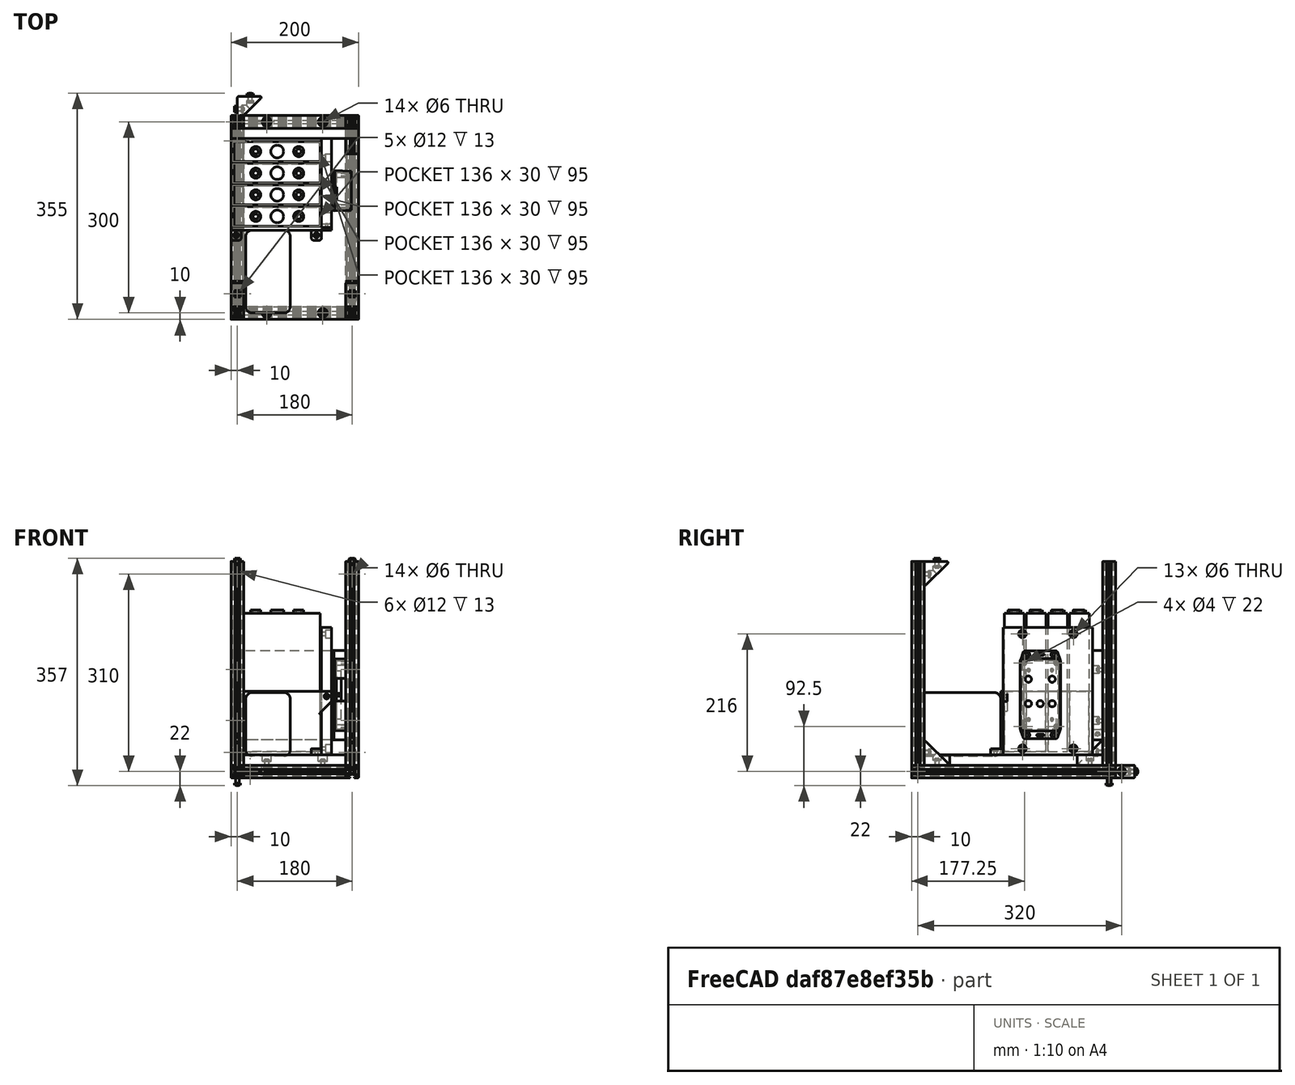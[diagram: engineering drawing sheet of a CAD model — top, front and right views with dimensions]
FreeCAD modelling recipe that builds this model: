
FCSTD DOCUMENT  (FreeCAD 0.17R9796 (Git))
Label: UPKframeNG2e
License: All rights reserved
LicenseURL: http://en.wikipedia.org/wiki/All_rights_reserved
objects: Part::Feature×64, Part::FeaturePython×24, Part::Compound×12, App::FeaturePython×8, App::Part×6, Part::Cylinder×5, Part::Box×4, Part::Cut×4, PartDesign::Body×2, PartDesign::Pocket×1, Part::Fillet×1, Part::MultiFuse×1
note: 119 computed .brp shape members not serialized (recipe doc carries the construction recipe); baked Part::Feature solids carry a one-line shape summary decoded from their .brp

FEATURE [Part::Feature] Pocket003001  label="tslot32con"
  Placement = pos=(0,10,10) rot=(1,0,0;1.5708rad)
  shape: bbox 20 x 320 x 20 mm, 150 faces (baked)
FEATURE [Part::Feature] Pocket003002  label="tslot16"
  Placement = pos=(10,0,10) rot=(0,1,0;1.5708rad)
  shape: bbox 160 x 20 x 20 mm, 94 faces (baked)
FEATURE [Part::Feature] Pocket003006  label="tslot16_001"
  Placement = pos=(10,-300,10) rot=(0,1,0;1.5708rad)
  shape: bbox 160 x 20 x 20 mm, 94 faces (baked)
FEATURE [Part::Feature] Pocket003007  label="tslot32con_001"
  Placement = pos=(180,-310,10) rot=(0,0.707107,0.707107;3.14159rad)
  shape: bbox 20 x 320 x 20 mm, 150 faces (baked)
FEATURE [Part::FeaturePython] Screw  label="M6x25-Screw"  # Fasteners workbench fastener (typed FeaturePython)
  Placement = pos=(-4,0,10) rot=(0,-1,0;1.5708rad)
  diameter = 7
  invert = false
  length = 6
  matchOuter = false
  offset = 0
  thread = false
  type = 15
FEATURE [Part::FeaturePython] Screw001  label="M6x25-Screw004"  # Fasteners workbench fastener (typed FeaturePython)
  Placement = pos=(-4,-300,10) rot=(0,-1,0;1.5708rad)
  diameter = 7
  invert = false
  length = 6
  matchOuter = false
  offset = 0
  thread = false
  type = 15
FEATURE [Part::FeaturePython] Screw002  label="M6x25-Screw005"  # Fasteners workbench fastener (typed FeaturePython)
  Placement = pos=(184,0,10) rot=(0,1,0;1.5708rad)
  diameter = 7
  invert = false
  length = 6
  matchOuter = false
  offset = 0
  thread = false
  type = 15
FEATURE [Part::FeaturePython] Screw004  label="M6x25-Screw006"  # Fasteners workbench fastener (typed FeaturePython)
  Placement = pos=(184,-300,10) rot=(0,1,0;1.5708rad)
  diameter = 7
  invert = false
  length = 6
  matchOuter = false
  offset = 0
  thread = false
  type = 15
FEATURE [App::Part] Part  label="lower_frame"
  Group = -> [Pocket003001,Pocket003002,Pocket003006,Pocket003007,Screw,Screw001,Screw002,Screw004]
  License = CC BY 3.0
  LicenseURL = http://creativecommons.org/licenses/by/3.0/
  Origin = -> PartOrigin
FEATURE [Part::Feature] Pocket003008  label="tslot32con001"
  Placement = pos=(0,10,10) rot=(1,0,0;1.5708rad)
  shape: bbox 20 x 320 x 20 mm, 150 faces (baked)
FEATURE [Part::Feature] Pocket003009  label="tslot041"
  Placement = pos=(10,0,10) rot=(0,1,0;1.5708rad)
  shape: bbox 160 x 20 x 20 mm, 94 faces (baked)
FEATURE [Part::Feature] Pocket003010  label="tslot16_002"
  Placement = pos=(10,-300,10) rot=(0,1,0;1.5708rad)
  shape: bbox 160 x 20 x 20 mm, 94 faces (baked)
FEATURE [Part::Feature] Pocket003011  label="tslot32con_002"
  Placement = pos=(180,-310,10) rot=(0,0.707107,0.707107;3.14159rad)
  shape: bbox 20 x 320 x 20 mm, 150 faces (baked)
FEATURE [Part::FeaturePython] Screw005  label="M6x25-Screw007"  # Fasteners workbench fastener (typed FeaturePython)
  Placement = pos=(-4,0,10) rot=(0,-1,0;1.5708rad)
  diameter = 7
  invert = false
  length = 6
  matchOuter = false
  offset = 0
  thread = false
  type = 15
FEATURE [Part::FeaturePython] Screw006  label="M6x25-Screw008"  # Fasteners workbench fastener (typed FeaturePython)
  Placement = pos=(-4,-300,10) rot=(0,-1,0;1.5708rad)
  diameter = 7
  invert = false
  length = 6
  matchOuter = false
  offset = 0
  thread = false
  type = 15
FEATURE [Part::FeaturePython] Screw007  label="M6x25-Screw009"  # Fasteners workbench fastener (typed FeaturePython)
  Placement = pos=(184,0,10) rot=(0,1,0;1.5708rad)
  diameter = 7
  invert = false
  length = 6
  matchOuter = false
  offset = 0
  thread = false
  type = 15
FEATURE [Part::FeaturePython] Screw008  label="M6x25-Screw010"  # Fasteners workbench fastener (typed FeaturePython)
  Placement = pos=(184,-300,10) rot=(0,1,0;1.5708rad)
  diameter = 7
  invert = false
  length = 6
  matchOuter = false
  offset = 0
  thread = false
  type = 15
FEATURE [App::Part] Part001  label="upper_frame"
  Group = -> [Pocket003008,Pocket003009,Pocket003010,Pocket003011,Screw005,Screw006,Screw007,Screw008]
  License = CC BY 3.0
  LicenseURL = http://creativecommons.org/licenses/by/3.0/
  Origin = -> PartOrigin001
  Placement = pos=(0,0,340) rot=(0,0,1;0rad)
FEATURE [Part::Feature] Fillet004001  label="Fillet005"
  shape: bbox 37.5 x 37.5 x 20 mm, 26 faces (baked)
FEATURE [Part::FeaturePython] Screw009  label="M6x12-Screw"  # Fasteners workbench fastener (typed FeaturePython)
  Placement = pos=(7,20,10) rot=(0,1,0;1.5708rad)
  diameter = 4
  invert = false
  length = 1
  matchOuter = false
  offset = 0
  thread = false
  type = 20
FEATURE [Part::Feature] Body001  label="m6nutplate"
  Placement = pos=(-1.5,15,5) rot=(0,-1,0;1.5708rad)
  shape: bbox 3 x 10 x 10 mm, 9 faces (baked)
FEATURE [App::Part] Part002  label="cornerstonescrewnut"
  License = CC BY 3.0
  LicenseURL = http://creativecommons.org/licenses/by/3.0/
  Origin = -> PartOrigin002
  Placement = pos=(10,-50,20) rot=(0,-1,0;1.5708rad)
FEATURE [Part::FeaturePython] Screw010  label="M6x12-Screw001"  # Fasteners workbench fastener (typed FeaturePython)
  Placement = pos=(20,33,10) rot=(1,0,0;1.5708rad)
  diameter = 4
  invert = false
  length = 1
  matchOuter = false
  offset = 0
  thread = false
  type = 20
FEATURE [Part::Feature] Body002  label="m6nutplate001"
  Placement = pos=(15,41.5,5) rot=(0.57735,0.57735,0.57735;4.18879rad)
  shape: bbox 10 x 3 x 10 mm, 9 faces (baked)
FEATURE [Part::Feature] Fillet004002  label="Fillet006"
  shape: bbox 37.5 x 37.5 x 20 mm, 26 faces (baked)
FEATURE [Part::FeaturePython] Screw011  label="M6x12-Screw002"  # Fasteners workbench fastener (typed FeaturePython)
  Placement = pos=(7,20,10) rot=(0,1,0;1.5708rad)
  diameter = 4
  invert = false
  length = 1
  matchOuter = false
  offset = 0
  thread = false
  type = 20
FEATURE [Part::Feature] Body003  label="m6nutplate002"
  Placement = pos=(-1.5,15,5) rot=(0,-1,0;1.5708rad)
  shape: bbox 3 x 10 x 10 mm, 9 faces (baked)
FEATURE [Part::FeaturePython] Screw012  label="M6x12-Screw003"  # Fasteners workbench fastener (typed FeaturePython)
  Placement = pos=(20,33,10) rot=(1,0,0;1.5708rad)
  diameter = 4
  invert = false
  length = 1
  matchOuter = false
  offset = 0
  thread = false
  type = 20
FEATURE [Part::Feature] Body004  label="m6nutplate003"
  Placement = pos=(15,41.5,5) rot=(0.57735,0.57735,0.57735;4.18879rad)
  shape: bbox 10 x 3 x 10 mm, 9 faces (baked)
FEATURE [App::Part] Part003  label="cornerstonescrewnut001"
  Group = -> [Body003,Screw011,Fillet004002,Screw012,Body004,PartOrigin002,Body001,Screw009,Fillet004001,Screw010,Body002,Part002]
  License = CC BY 3.0
  LicenseURL = http://creativecommons.org/licenses/by/3.0/
  Origin = -> PartOrigin003
  Placement = pos=(190,-50,20) rot=(0,-1,0;1.5708rad)
FEATURE [Part::Feature] Fillet004003  label="Fillet007"
  shape: bbox 37.5 x 37.5 x 20 mm, 26 faces (baked)
FEATURE [Part::FeaturePython] Screw013  label="M6x12-Screw004"  # Fasteners workbench fastener (typed FeaturePython)
  Placement = pos=(7,20,10) rot=(0,1,0;1.5708rad)
  diameter = 4
  invert = false
  length = 1
  matchOuter = false
  offset = 0
  thread = false
  type = 20
FEATURE [Part::Feature] Body005  label="m6nutplate004"
  Placement = pos=(-1.5,15,5) rot=(0,-1,0;1.5708rad)
  shape: bbox 3 x 10 x 10 mm, 9 faces (baked)
FEATURE [Part::FeaturePython] Screw014  label="M6x12-Screw005"  # Fasteners workbench fastener (typed FeaturePython)
  Placement = pos=(20,33,10) rot=(1,0,0;1.5708rad)
  diameter = 4
  invert = false
  length = 1
  matchOuter = false
  offset = 0
  thread = false
  type = 20
FEATURE [Part::Feature] Body006  label="m6nutplate005"
  Placement = pos=(15,41.5,5) rot=(0.57735,0.57735,0.57735;4.18879rad)
  shape: bbox 10 x 3 x 10 mm, 9 faces (baked)
FEATURE [App::Part] Part004  label="cornerstonescrewnut002"
  Group = -> [Body005,Screw013,Fillet004003,Screw014,Body006]
  License = CC BY 3.0
  LicenseURL = http://creativecommons.org/licenses/by/3.0/
  Origin = -> PartOrigin004
  Placement = pos=(-10,-50,340) rot=(0,1,0;1.5708rad)
FEATURE [Part::Feature] Fillet004004  label="Fillet008"
  shape: bbox 37.5 x 37.5 x 20 mm, 26 faces (baked)
FEATURE [Part::FeaturePython] Screw015  label="M6x12-Screw006"  # Fasteners workbench fastener (typed FeaturePython)
  Placement = pos=(7,20,10) rot=(0,1,0;1.5708rad)
  diameter = 4
  invert = false
  length = 1
  matchOuter = false
  offset = 0
  thread = false
  type = 20
FEATURE [Part::Feature] Body007  label="m6nutplate006"
  Placement = pos=(-1.5,15,5) rot=(0,-1,0;1.5708rad)
  shape: bbox 3 x 10 x 10 mm, 9 faces (baked)
FEATURE [Part::FeaturePython] Screw016  label="M6x12-Screw007"  # Fasteners workbench fastener (typed FeaturePython)
  Placement = pos=(20,33,10) rot=(1,0,0;1.5708rad)
  diameter = 4
  invert = false
  length = 1
  matchOuter = false
  offset = 0
  thread = false
  type = 20
FEATURE [Part::Feature] Body008  label="m6nutplate007"
  Placement = pos=(15,41.5,5) rot=(0.57735,0.57735,0.57735;4.18879rad)
  shape: bbox 10 x 3 x 10 mm, 9 faces (baked)
FEATURE [App::Part] Part005  label="cornerstonescrewnut003"
  Group = -> [Body007,Screw015,Fillet004004,Screw016,Body008]
  License = CC BY 3.0
  LicenseURL = http://creativecommons.org/licenses/by/3.0/
  Origin = -> PartOrigin005
  Placement = pos=(170,-50,340) rot=(0,1,0;1.5708rad)
FEATURE [Part::Feature] Body009001  label="m6nutplate010"
  Placement = pos=(-1.5,15,5) rot=(0,-1,0;1.5708rad)
  shape: bbox 3 x 10 x 10 mm, 9 faces (baked)
FEATURE [Part::Feature] Body010001  label="m6nutplate011"
  Placement = pos=(15,41.5,5) rot=(0.57735,0.57735,0.57735;4.18879rad)
  shape: bbox 10 x 3 x 10 mm, 9 faces (baked)
FEATURE [Part::Feature] Screw018001  label="M6x12-Screw010"
  Placement = pos=(20,33,10) rot=(1,0,0;1.5708rad)
  shape: bbox 10.5 x 15.3 x 10.5 mm, 15 faces (baked)
FEATURE [Part::Feature] Screw017001  label="M6x12-Screw011"
  Placement = pos=(7,20,10) rot=(0,1,0;1.5708rad)
  shape: bbox 15.3 x 10.5 x 10.5 mm, 15 faces (baked)
FEATURE [Part::Feature] Fillet004005001  label="Fillet010"
  shape: bbox 37.5 x 37.5 x 20 mm, 26 faces (baked)
FEATURE [Part::Compound] Compound
  Links = -> [Body009001,Fillet004005001,Screw017001,Body010001,Screw018001]
  Placement = pos=(10,-250,340) rot=(0.707107,0,-0.707107;3.14159rad)
FEATURE [Part::Feature] Body010002  label="m6nutplate012"
  Placement = pos=(-1.5,15,5) rot=(0,-1,0;1.5708rad)
  shape: bbox 3 x 10 x 10 mm, 9 faces (baked)
FEATURE [Part::Feature] Body010003  label="m6nutplate013"
  Placement = pos=(15,41.5,5) rot=(0.57735,0.57735,0.57735;4.18879rad)
  shape: bbox 10 x 3 x 10 mm, 9 faces (baked)
FEATURE [Part::Feature] Screw018002  label="M6x12-Screw012"
  Placement = pos=(20,33,10) rot=(1,0,0;1.5708rad)
  shape: bbox 10.5 x 15.3 x 10.5 mm, 15 faces (baked)
FEATURE [Part::Feature] Screw018003  label="M6x12-Screw013"
  Placement = pos=(7,20,10) rot=(0,1,0;1.5708rad)
  shape: bbox 15.3 x 10.5 x 10.5 mm, 15 faces (baked)
FEATURE [Part::Feature] Fillet004005002  label="Fillet011"
  shape: bbox 37.5 x 37.5 x 20 mm, 26 faces (baked)
FEATURE [Part::Compound] Compound001
  Links = -> [Body010002,Fillet004005002,Screw018003,Body010003,Screw018002]
  Placement = pos=(190,-250,340) rot=(0.707107,0,-0.707107;3.14159rad)
FEATURE [Part::Feature] Body010004  label="m6nutplate014"
  Placement = pos=(-1.5,15,5) rot=(0,-1,0;1.5708rad)
  shape: bbox 3 x 10 x 10 mm, 9 faces (baked)
FEATURE [Part::Feature] Body010005  label="m6nutplate015"
  Placement = pos=(15,41.5,5) rot=(0.57735,0.57735,0.57735;4.18879rad)
  shape: bbox 10 x 3 x 10 mm, 9 faces (baked)
FEATURE [Part::Feature] Screw018004  label="M6x12-Screw014"
  Placement = pos=(20,33,10) rot=(1,0,0;1.5708rad)
  shape: bbox 10.5 x 15.3 x 10.5 mm, 15 faces (baked)
FEATURE [Part::Feature] Screw018005  label="M6x12-Screw015"
  Placement = pos=(7,20,10) rot=(0,1,0;1.5708rad)
  shape: bbox 15.3 x 10.5 x 10.5 mm, 15 faces (baked)
FEATURE [Part::Feature] Fillet004005003  label="Fillet012"
  shape: bbox 37.5 x 37.5 x 20 mm, 26 faces (baked)
FEATURE [Part::Compound] Compound002
  Links = -> [Body010004,Fillet004005003,Screw018005,Body010005,Screw018004]
  Placement = pos=(10,-290,60) rot=(0.57735,0.57735,-0.57735;4.18879rad)
FEATURE [Part::Feature] Body010006  label="m6nutplate016"
  Placement = pos=(-1.5,15,5) rot=(0,-1,0;1.5708rad)
  shape: bbox 3 x 10 x 10 mm, 9 faces (baked)
FEATURE [Part::Feature] Body010007  label="m6nutplate017"
  Placement = pos=(15,41.5,5) rot=(0.57735,0.57735,0.57735;4.18879rad)
  shape: bbox 10 x 3 x 10 mm, 9 faces (baked)
FEATURE [Part::Feature] Screw018006  label="M6x12-Screw016"
  Placement = pos=(20,33,10) rot=(1,0,0;1.5708rad)
  shape: bbox 10.5 x 15.3 x 10.5 mm, 15 faces (baked)
FEATURE [Part::Feature] Screw018007  label="M6x12-Screw017"
  Placement = pos=(7,20,10) rot=(0,1,0;1.5708rad)
  shape: bbox 15.3 x 10.5 x 10.5 mm, 15 faces (baked)
FEATURE [Part::Feature] Fillet004005004  label="Fillet013"
  shape: bbox 37.5 x 37.5 x 20 mm, 26 faces (baked)
FEATURE [Part::Compound] Compound003
  Links = -> [Body010006,Fillet004005004,Screw018007,Body010007,Screw018006]
  Placement = pos=(190,-290,60) rot=(0.57735,0.57735,-0.57735;4.18879rad)
FEATURE [Part::Feature] Pocket001001  label="tslot32"
  Placement = pos=(0,0,20) rot=(0,0,1;0rad)
  shape: bbox 20 x 20 x 320 mm, 94 faces (baked)
FEATURE [Part::Feature] Body010008  label="m6nutplate018"
  Placement = pos=(-1.5,15,5) rot=(0,-1,0;1.5708rad)
  shape: bbox 3 x 10 x 10 mm, 9 faces (baked)
FEATURE [Part::Feature] Body010009  label="m6nutplate019"
  Placement = pos=(15,41.5,5) rot=(0.57735,0.57735,0.57735;4.18879rad)
  shape: bbox 10 x 3 x 10 mm, 9 faces (baked)
FEATURE [Part::Feature] Screw018008  label="M6x12-Screw018"
  Placement = pos=(20,33,10) rot=(1,0,0;1.5708rad)
  shape: bbox 10.5 x 15.3 x 10.5 mm, 15 faces (baked)
FEATURE [Part::Feature] Screw018009  label="M6x12-Screw019"
  Placement = pos=(7,20,10) rot=(0,1,0;1.5708rad)
  shape: bbox 15.3 x 10.5 x 10.5 mm, 15 faces (baked)
FEATURE [Part::Feature] Fillet004005005  label="Fillet014"
  shape: bbox 37.5 x 37.5 x 20 mm, 26 faces (baked)
FEATURE [Part::Compound] Compound004
  Links = -> [Body010008,Fillet004005005,Screw018009,Body010009,Screw018008]
  Placement = pos=(-10,-10,60) rot=(0.57735,-0.57735,0.57735;4.18879rad)
FEATURE [Part::Feature] Pocket003012  label="tslot32_001"
  Placement = pos=(0,-300,20) rot=(0,0,1;0rad)
  shape: bbox 20 x 20 x 320 mm, 94 faces (baked)
FEATURE [Part::Feature] Pocket003013  label="tslot32_002"
  Placement = pos=(180,0,20) rot=(0,0,1;0rad)
  shape: bbox 20 x 20 x 320 mm, 94 faces (baked)
FEATURE [Part::Feature] Pocket003014  label="tslot32_003"
  Placement = pos=(180,-300,20) rot=(0,0,1;0rad)
  shape: bbox 20 x 20 x 320 mm, 94 faces (baked)
FEATURE [PartDesign::Body] Body010027
FEATURE [Part::FeaturePython] Screw018021  label="M6x12-Screw032"  # Fasteners workbench fastener (typed FeaturePython)
  diameter = 4
  invert = false
  length = 1
  matchOuter = false
  offset = 0
  thread = false
  type = 20
FEATURE [Part::Feature] Body010028  label="m6nutplate032"
  Placement = pos=(5,-5,-8.39) rot=(0,1,0;3.14159rad)
  shape: bbox 10 x 10 x 3 mm, 9 faces (baked)
FEATURE [App::FeaturePython] circularEdgeConstraint009  # a2plus constraint (typed FeaturePython)
  Object1 = Screw
  Object2 = Body001
  SubElement1 = Edge7
  SubElement2 = Edge20
  Type = circularEdge
  directionConstraint = 1
  lockRotation = false
  offset = 0
FEATURE [Part::Compound] Compound017  label="nutplate12screw008"
  Links = -> [Screw018021,circularEdgeConstraint009,Body010028]
  Placement = pos=(10,30,6) rot=(0,0,1;0rad)
FEATURE [Part::FeaturePython] Screw018022  label="M6x12-Screw033"  # Fasteners workbench fastener (typed FeaturePython)
  diameter = 4
  invert = false
  length = 1
  matchOuter = false
  offset = 0
  thread = false
  type = 20
FEATURE [Part::Feature] Body010029  label="m6nutplate033"
  Placement = pos=(5,-5,-8.39) rot=(0,1,0;3.14159rad)
  shape: bbox 10 x 10 x 3 mm, 9 faces (baked)
FEATURE [App::FeaturePython] circularEdgeConstraint010  # a2plus constraint (typed FeaturePython)
  Object1 = Screw
  Object2 = Body001
  SubElement1 = Edge7
  SubElement2 = Edge20
  Type = circularEdge
  directionConstraint = 1
  lockRotation = false
  offset = 0
FEATURE [Part::Compound] Compound018  label="nutplate12screw009"
  Links = -> [Screw018022,circularEdgeConstraint010,Body010029]
  Placement = pos=(10,110,6) rot=(0,0,1;0rad)
FEATURE [Part::FeaturePython] Screw018023  label="M6x12-Screw034"  # Fasteners workbench fastener (typed FeaturePython)
  diameter = 4
  invert = false
  length = 1
  matchOuter = false
  offset = 0
  thread = false
  type = 20
FEATURE [Part::Feature] Body010030  label="m6nutplate034"
  Placement = pos=(5,-5,-8.39) rot=(0,1,0;3.14159rad)
  shape: bbox 10 x 10 x 3 mm, 9 faces (baked)
FEATURE [App::FeaturePython] circularEdgeConstraint011  # a2plus constraint (typed FeaturePython)
  Object1 = Screw
  Object2 = Body001
  SubElement1 = Edge7
  SubElement2 = Edge20
  Type = circularEdge
  directionConstraint = 1
  lockRotation = false
  offset = 0
FEATURE [Part::Compound] Compound019  label="nutplate12screw010"
  Links = -> [Screw018023,circularEdgeConstraint011,Body010030]
  Placement = pos=(190,110,6) rot=(0,0,1;0rad)
FEATURE [Part::FeaturePython] Screw018024  label="M6x12-Screw035"  # Fasteners workbench fastener (typed FeaturePython)
  diameter = 4
  invert = false
  length = 1
  matchOuter = false
  offset = 0
  thread = false
  type = 20
FEATURE [Part::Feature] Body010031  label="m6nutplate035"
  Placement = pos=(5,-5,-8.39) rot=(0,1,0;3.14159rad)
  shape: bbox 10 x 10 x 3 mm, 9 faces (baked)
FEATURE [App::FeaturePython] circularEdgeConstraint012  # a2plus constraint (typed FeaturePython)
  Object1 = Screw
  Object2 = Body001
  SubElement1 = Edge7
  SubElement2 = Edge20
  Type = circularEdge
  directionConstraint = 1
  lockRotation = false
  offset = 0
FEATURE [Part::Compound] Compound020  label="nutplate12screw011"
  Links = -> [Screw018024,circularEdgeConstraint012,Body010031]
  Placement = pos=(190,30,6) rot=(0,0,1;0rad)
FEATURE [Part::Compound] Compound021  label="front_plate"
  Links = -> [Body010027,Compound020,Compound019,Compound017,Compound018]
  Placement = pos=(-10,-10,60) rot=(1,0,0;1.5708rad)
FEATURE [Part::Compound] Compound016  label="bottom_plate"
  Placement = pos=(190,-310,20) rot=(0,0,1;1.5708rad)
FEATURE [PartDesign::Pocket] Pocket003019
  Length = 10
  Placement = pos=(130,-166,235) rot=(0,1,0;1.5708rad)
  Type = 0
FEATURE [Part::Box] Box003  label="MPPT"
  AttacherType = Attacher::AttachEngine3D
  Height = 100
  Length = 130
  Placement = pos=(290,128,10) rot=(0,0,1;0rad)
  Width = 70
FEATURE [Part::Fillet] Fillet007  label="MPPT               "
  Base = -> Box003
  Edges = 12 edges r=10: [Edge1,Edge2,Edge3,Edge4,Edge5,Edge6,Edge7,Edge8,Edge9,Edge10,Edge11,Edge12]
  Placement = pos=(211,-590,24) rot=(0,0,1;1.5708rad)
FEATURE [Part::Feature] Part__Feature1213  label="1591XXBF LID"
  Placement = pos=(153,-86,180) rot=(-0.57735,0.57735,0.57735;4.18879rad)
  shape: bbox 12.61 x 63.32 x 138 mm, 220 faces (baked)
FEATURE [Part::Feature] Part__Feature1212  label="1591XXB BOX"
  Placement = pos=(0,0,0) rot=(0,0.707107,0.707107;3.14159rad)
  shape: bbox 113.8 x 28.25 x 63.32 mm, 133 faces (baked)
FEATURE [Part::Cylinder] Cylinder  label="Zylinder"
  Angle = 360
  AttacherType = Attacher::AttachEngine3D
  Height = 60
  Placement = pos=(-14,48,18.6) rot=(1,0,0;1.5708rad)
  Radius = 5
FEATURE [Part::Cylinder] Cylinder001  label="Zylinder001"
  Angle = 360
  AttacherType = Attacher::AttachEngine3D
  Height = 60
  Placement = pos=(-14,48,0) rot=(1,0,0;1.5708rad)
  Radius = 5
FEATURE [Part::Cylinder] Cylinder002  label="Zylinder002"
  Angle = 360
  AttacherType = Attacher::AttachEngine3D
  Height = 60
  Placement = pos=(-14,48,-18.66) rot=(1,0,0;1.5708rad)
  Radius = 5
FEATURE [Part::Cylinder] Cylinder003  label="Zylinder003"
  Angle = 360
  AttacherType = Attacher::AttachEngine3D
  Height = 60
  Placement = pos=(24.49,48,18.6) rot=(1,0,0;1.5708rad)
  Radius = 5
FEATURE [Part::Cylinder] Cylinder004  label="Zylinder004"
  Angle = 360
  AttacherType = Attacher::AttachEngine3D
  Height = 60
  Placement = pos=(24.49,48,-18.66) rot=(1,0,0;1.5708rad)
  Radius = 5
FEATURE [Part::MultiFuse] Fusion
  Shapes = -> [Cylinder,Cylinder004,Cylinder003,Cylinder002,Cylinder001]
FEATURE [Part::Cut] Cut
  Base = -> Part__Feature1212
  Tool = -> Fusion
FEATURE [Part::Box] Box002  label="Würfel002"
  AttacherType = Attacher::AttachEngine3D
  Height = 10
  Length = 76
  Placement = pos=(-38,16,-36) rot=(0,0,1;0rad)
  Width = 12.6
FEATURE [Part::Cut] Cut001
  Base = -> Cut
  Tool = -> Box002
FEATURE [Part::Box] Box004  label="Würfel003"
  AttacherType = Attacher::AttachEngine3D
  Height = 10
  Length = 36
  Placement = pos=(-10,9,24) rot=(0,0,1;0rad)
  Width = 20
FEATURE [Part::Cut] Cut002
  Base = -> Cut001
  Tool = -> Box004
FEATURE [Part::Box] Box  label="Würfel"
  AttacherType = Attacher::AttachEngine3D
  Height = 20
  Length = 10
  Placement = pos=(49,23,-6) rot=(0,0,1;0rad)
  Width = 6
FEATURE [Part::Cut] Cut003  label="bms-cover"
  Base = -> Cut002
  Placement = pos=(179,-108,130.5) rot=(0.57735,-0.57735,0.57735;2.0944rad)
  Tool = -> Box
FEATURE [PartDesign::Body] Body010032
FEATURE [Part::FeaturePython] Screw018025  label="M6x12-Screw036"  # Fasteners workbench fastener (typed FeaturePython)
  diameter = 4
  invert = false
  length = 1
  matchOuter = false
  offset = 0
  thread = false
  type = 20
FEATURE [App::FeaturePython] circularEdgeConstraint013  # a2plus constraint (typed FeaturePython)
  Object1 = Screw
  Object2 = Body001
  SubElement1 = Edge7
  SubElement2 = Edge20
  Type = circularEdge
  directionConstraint = 1
  lockRotation = false
  offset = 0
FEATURE [Part::FeaturePython] Screw018026  label="M6x12-Screw037"  # Fasteners workbench fastener (typed FeaturePython)
  diameter = 4
  invert = false
  length = 1
  matchOuter = false
  offset = 0
  thread = false
  type = 20
FEATURE [Part::Feature] Body010034  label="m6nutplate037"
  Placement = pos=(5,-5,-8.39) rot=(0,1,0;3.14159rad)
  shape: bbox 10 x 10 x 3 mm, 9 faces (baked)
FEATURE [App::FeaturePython] circularEdgeConstraint014  # a2plus constraint (typed FeaturePython)
  Object1 = Screw
  Object2 = Body001
  SubElement1 = Edge7
  SubElement2 = Edge20
  Type = circularEdge
  directionConstraint = 1
  lockRotation = false
  offset = 0
FEATURE [Part::FeaturePython] Screw018027  label="M6x12-Screw038"  # Fasteners workbench fastener (typed FeaturePython)
  diameter = 4
  invert = false
  length = 1
  matchOuter = false
  offset = 0
  thread = false
  type = 20
FEATURE [Part::Feature] Body010035  label="m6nutplate038"
  Placement = pos=(5,-5,-8.39) rot=(0,1,0;3.14159rad)
  shape: bbox 10 x 10 x 3 mm, 9 faces (baked)
FEATURE [App::FeaturePython] circularEdgeConstraint015  # a2plus constraint (typed FeaturePython)
  Object1 = Screw
  Object2 = Body001
  SubElement1 = Edge7
  SubElement2 = Edge20
  Type = circularEdge
  directionConstraint = 1
  lockRotation = false
  offset = 0
FEATURE [Part::FeaturePython] Screw018028  label="M6x12-Screw039"  # Fasteners workbench fastener (typed FeaturePython)
  diameter = 4
  invert = false
  length = 1
  matchOuter = false
  offset = 0
  thread = false
  type = 20
FEATURE [Part::Feature] Body010036  label="m6nutplate039"
  Placement = pos=(5,-5,-8.39) rot=(0,1,0;3.14159rad)
  shape: bbox 10 x 10 x 3 mm, 9 faces (baked)
FEATURE [App::FeaturePython] circularEdgeConstraint016  # a2plus constraint (typed FeaturePython)
  Object1 = Screw
  Object2 = Body001
  SubElement1 = Edge7
  SubElement2 = Edge20
  Type = circularEdge
  directionConstraint = 1
  lockRotation = false
  offset = 0
FEATURE [Part::Compound] Compound026  label="bmsmounting_plate"
  Links = -> [Body010032]
  Placement = pos=(132,-26,36) rot=(0.707107,0,0.707107;3.14159rad)
FEATURE [Part::Feature] Body010037  label="batterymount"
  Placement = pos=(-10,-170,36) rot=(0,0,1;0rad)
  shape: bbox 158 x 176 x 100 mm, 72 faces (baked)
FEATURE [Part::Feature] Body010033  label="m6nutplate036"
  Placement = pos=(5,-5,-8.39) rot=(0,1,0;3.14159rad)
  shape: bbox 10 x 10 x 3 mm, 9 faces (baked)
FEATURE [Part::Feature] Body010038  label="cam72"
  Placement = pos=(130,-62,41) rot=(0,0,1;1.5708rad)
  shape: bbox 135.1 x 31 x 222.5 mm, 16 faces (baked)
FEATURE [Part::Feature] Body010039  label="cam72_001"
  Placement = pos=(130,-96,41) rot=(0,0,1;1.5708rad)
  shape: bbox 135.1 x 31 x 222.5 mm, 16 faces (baked)
FEATURE [Part::Feature] Body010040  label="cam72_002"
  Placement = pos=(130,-130,41) rot=(0,0,1;1.5708rad)
  shape: bbox 135.1 x 31 x 222.5 mm, 16 faces (baked)
FEATURE [Part::Feature] Body010041  label="cam72_003"
  Placement = pos=(130,-164,41) rot=(0,0,1;1.5708rad)
  shape: bbox 135.1 x 31 x 222.5 mm, 16 faces (baked)
